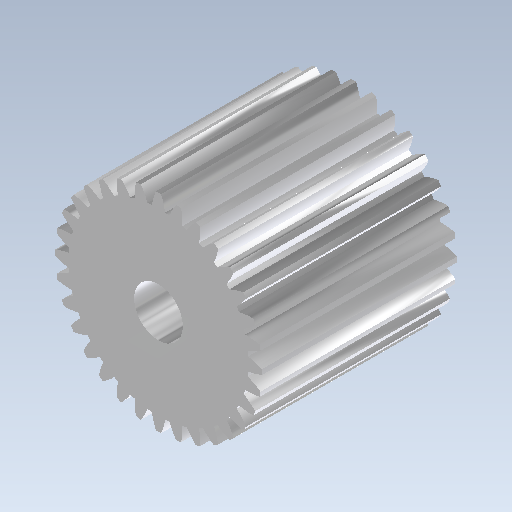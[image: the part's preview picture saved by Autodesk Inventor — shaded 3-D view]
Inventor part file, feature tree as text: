
AUTODESK INVENTOR PART (.ipt)
format: ipt  version: 2021 (Build 250183000, 183)  size: 339,456 bytes
history: native  units: mm (DEFAULTED — no unit token found)
features: plane x3, other x3, sketch x3, extrude x2
ambient origin geometry x8: Origin, YZ Plane, XZ Plane, XY Plane, X Axis, Y Axis, Z Axis, Center Point
bodies: Solid1 (feature_tree)
feature tree (11):
  extrude  "Extrusion1"  Depth=40.0mm TaperAngle=0.0deg
  plane  "Work Plane2"
  plane  "Work Plane8"
  plane  "Work Plane9"
  other  "Spur Gear"
  extrude  "Extrusion2"  Depth=10.0mm TaperAngle=0.0deg
  sketch  "Sketch1"  dims[d0=42.5mm d1=40.0mm d2=0.0mm]
  sketch  "Sketch2"  dims[d3=40.0mm d4=10.0mm d5=0.0mm]
  other  "Srf1"
  sketch  "Sketch3"  dims[d16=80.0mm d17=0.0mm d34=0.981748mm d39=0.0mm d41=0.0mm d43=80.0mm d46=80.0mm d47=0.0mm d48=0.0mm d49=10.0mm d50=40.0mm d51=0.0mm]
  other  "Pitch Diameter"
